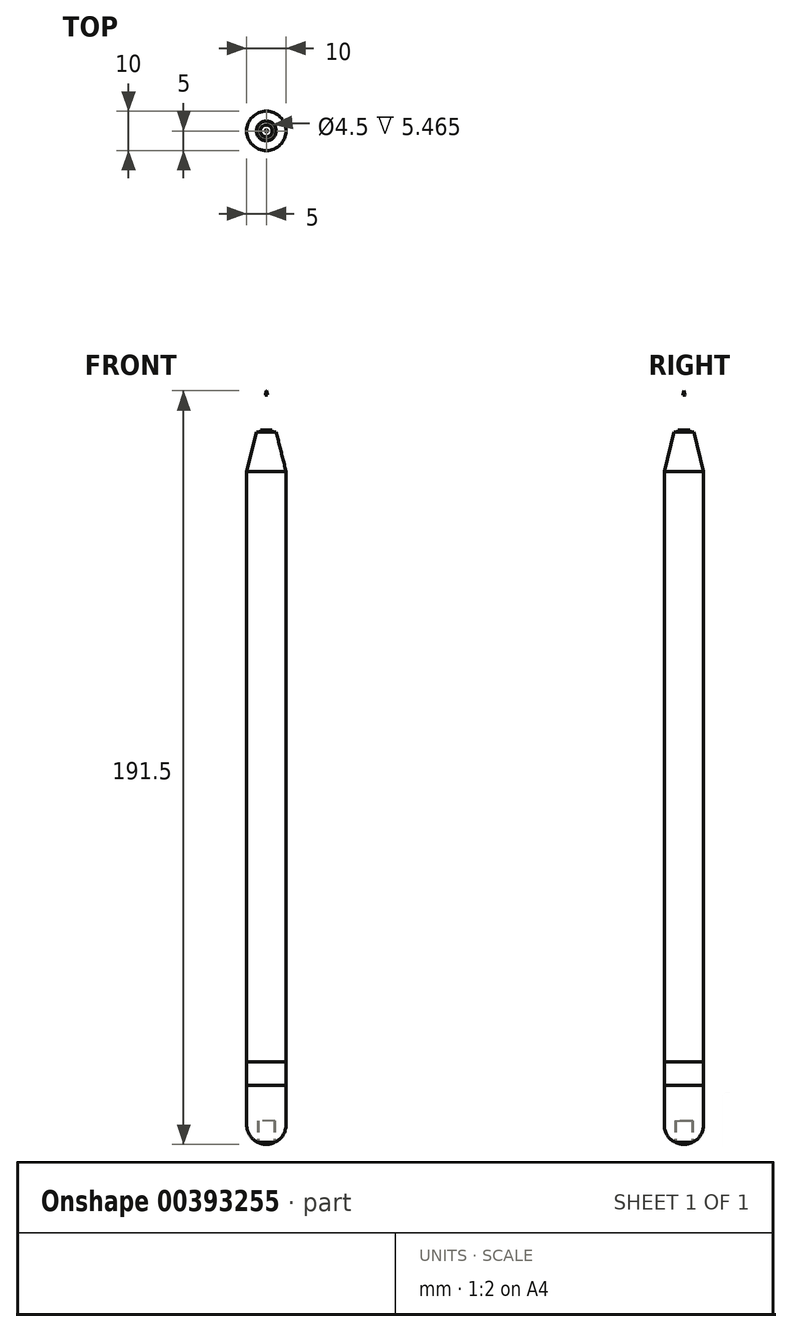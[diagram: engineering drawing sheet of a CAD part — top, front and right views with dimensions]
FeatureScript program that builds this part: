
annotation { "Feature Type Name" : "Feature", "Feature Type Description" : "" }
export const myFeature = defineFeature(function(context is Context, id is Id, definition is map)
    precondition{}
    {
        {
            var Q0;
            Q0=qCreatedBy(makeId("Top.planeOp"),FACE);
            var sketch = newSketch(context, id + "F0", { "sketchPlane" : qUnion([Q0])});
            skCircle(sketch, "E0", {"center": v(0, 0) * mm, "radius": 5 * mm});
            skSolve(sketch);
        }
        {
            var Q0;
            Q0 = qSketchRegion(id + "F0", true);
            extrude(context, id + "F1", {"entities" : qUnion([Q0]), "endBound" : BoundingType.SYMMETRIC, "depth" : 150 * mm});
        }
        {
            var Q0;
            Q0=qCreatedBy(makeId("Front.planeOp"),FACE);
            var sketch = newSketch(context, id + "F2", { "sketchPlane" : qUnion([Q0])});
            skLineSegment(sketch, "E1", {"start": v(0, 85) * mm, "end": v(0, 75) * mm, "construction": true});
            skLineSegment(sketch, "E2.0", {"start": v(-5, 75) * mm, "end": v(5, 75) * mm, "construction": true});
            skLineSegment(sketch, "E3", {"start": v(-5, -75) * mm, "end": v(-5, 75) * mm, "construction": true});
            skLineSegment(sketch, "E4", {"start": v(5, 75) * mm, "end": v(5, -75) * mm, "construction": true});
            skLineSegment(sketch, "E5", {"start": v(-5, 75) * mm, "end": v(0, 75) * mm});
            skLineSegment(sketch, "E6", {"start": v(0, 85) * mm, "end": v(0, 75) * mm});
            skLineSegment(sketch, "E7", {"start": v(-5, 85) * mm, "end": v(-5, 75) * mm, "construction": true});
            skLineSegment(sketch, "E8", {"start": v(-5, 85) * mm, "end": v(0, 85) * mm, "construction": true});
            skLineSegment(sketch, "E9", {"start": v(-5, 75) * mm, "end": v(-2.5, 85) * mm});
            skLineSegment(sketch, "E10", {"start": v(-2.5, 85) * mm, "end": v(0, 85) * mm});
            skSolve(sketch);
        }
        {
            var Q0;
            Q0 = qSketchRegion(id + "F2", true);
            var Q1;
            Q1=sQuery(id+"F2.wireOp",EDGE,"E1");
            revolve(context, id + "F3", {"operationType" : NewBodyOperationType.ADD, "entities" : qUnion([Q0]), "axis" : qUnion([Q1]), "revolveType" : RevolveType.FULL});
        }
        {
            var Q0;
            Q0=qCreatedBy(makeId("Front.planeOp"),FACE);
            var sketch = newSketch(context, id + "F4", { "sketchPlane" : qUnion([Q0])});
            skLineSegment(sketch, "E11", {"start": v(-2.5, 85.5) * mm, "end": v(0, 95.5) * mm});
            skLineSegment(sketch, "E12", {"start": v(0, 95.5) * mm, "end": v(0, 85.5) * mm});
            skLineSegment(sketch, "E13", {"start": v(-2.5, 85.5) * mm, "end": v(0, 85.5) * mm});
            skLineSegment(sketch, "E14", {"start": v(-1.5, 85.5) * mm, "end": v(-1.5, 85) * mm});
            skLineSegment(sketch, "E15", {"start": v(-1.5, 85) * mm, "end": v(0, 85) * mm});
            skLineSegment(sketch, "E16", {"start": v(0, 85) * mm, "end": v(0, 85.5) * mm});
            skArc(sketch, "E17", {"start": v(-0.3, 94.34) * mm, "mid": v(-0.18, 94.5) * mm, "end": v(0, 94.56) * mm});
            skSolve(sketch);
        }
        {
            var Q0;
            {var subQ2=sQuery(id+"F4.wireOp",EDGE,"E14");Q0=makeQuery(id+"F4.imprint","IMPRINT",FACE,{"disambiguationData":[TD([[makeQuery(id+"F4.imprint","IMPRINT",EDGE,{"derivedFrom":subQ2}),1.0]])]});}
            var Q1;
            {var subQ6=sQuery(id+"F4.wireOp",EDGE,"E17");Q1=makeQuery(id+"F4.imprint","IMPRINT",FACE,{"disambiguationData":[TD([[makeQuery(id+"F4.imprint","IMPRINT",EDGE,{"derivedFrom":subQ6}),-1.0]])]});}
            var Q2;
            Q2=sQuery(id+"F4.wireOp",EDGE,"E12");
            revolve(context, id + "F5", {"entities" : qUnion([Q0, Q1]), "axis" : qUnion([Q2]), "revolveType" : RevolveType.FULL});
        }
        {
            var Q0;
            Q0=qCreatedBy(makeId("Front.planeOp"),FACE);
            var sketch = newSketch(context, id + "F6", { "sketchPlane" : qUnion([Q0])});
            skLineSegment(sketch, "E18", {"start": v(0, -81) * mm, "end": v(0, -74.97) * mm});
            skLineSegment(sketch, "E19", {"start": v(0, -81) * mm, "end": v(5, -81) * mm});
            skLineSegment(sketch, "E20", {"start": v(5, -81) * mm, "end": v(5, -75) * mm});
            skLineSegment(sketch, "E21.0", {"start": v(-5, -75) * mm, "end": v(5, -75) * mm});
            skSolve(sketch);
        }
        {
            var Q0;
            Q0 = qSketchRegion(id + "F6", true);
            var Q1;
            Q1=sQuery(id+"F6.wireOp",EDGE,"E18");
            revolve(context, id + "F7", {"entities" : qUnion([Q0]), "axis" : qUnion([Q1]), "revolveType" : RevolveType.FULL});
        }
        {
            var Q0;
            Q0=qCreatedBy(makeId("Front.planeOp"),FACE);
            var sketch = newSketch(context, id + "F8", { "sketchPlane" : qUnion([Q0])});
            skLineSegment(sketch, "E22.bottom", {"start": v(0, -96) * mm, "end": v(-5, -96) * mm});
            skLineSegment(sketch, "E22.top", {"start": v(0, -81) * mm, "end": v(-5, -81) * mm});
            skLineSegment(sketch, "E22.left", {"start": v(0, -96) * mm, "end": v(0, -81) * mm});
            skLineSegment(sketch, "E22.right", {"start": v(-5, -96) * mm, "end": v(-5, -81) * mm});
            skLineSegment(sketch, "E23.0", {"start": v(5, -81) * mm, "end": v(-5, -81) * mm, "construction": true});
            skArc(sketch, "E24", {"start": v(0, -96) * mm, "mid": v(-3.54, -94.54) * mm, "end": v(-5, -91) * mm});
            skSolve(sketch);
        }
        {
            var Q0;
            {var subQ0=sQuery(id+"F8.wireOp",EDGE,"E22.top");Q0=makeQuery(id+"F8.imprint","IMPRINT",FACE,{"disambiguationData":[TD([[makeQuery(id+"F8.imprint","IMPRINT",EDGE,{"derivedFrom":subQ0}),1.0]])]});}
            var Q1;
            Q1=sQuery(id+"F8.wireOp",EDGE,"E22.left");
            revolve(context, id + "F9", {"entities" : qUnion([Q0]), "axis" : qUnion([Q1]), "revolveType" : RevolveType.FULL});
        }
        {
            var Q0;
            Q0=qCreatedBy(makeId("Top.planeOp"),FACE);
            cPlane(context, id + "F10", {"entities" : qUnion([Q0]), "cplaneType" : CPlaneType.OFFSET, "offset" : 95 * mm, "oppositeDirection" : true, "width" : 150 * mm, "height" : 150 * mm});
        }
        {
            var Q0;
            Q0=qCreatedBy(id+"F10.planeOp",FACE);
            var sketch = newSketch(context, id + "F11", { "sketchPlane" : qUnion([Q0])});
            skCircle(sketch, "E25", {"center": v(0, 0) * mm, "radius": 2.25 * mm});
            skCircle(sketch, "E26", {"center": v(0, 0) * mm, "radius": 2 * mm});
            skSolve(sketch);
        }
        {
            var Q0;
            Q0 = qSketchRegion(id + "F11", true);
            extrude(context, id + "F12", {"entities" : qUnion([Q0]), "operationType" : NewBodyOperationType.REMOVE, "depth" : 5 * mm, "hasSecondDirection" : true, "secondDirectionOppositeDirection" : true, "secondDirectionDepth" : 25 * mm});
        }
    });
